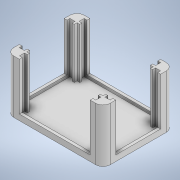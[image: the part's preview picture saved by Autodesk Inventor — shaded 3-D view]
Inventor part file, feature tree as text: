
AUTODESK INVENTOR PART (.ipt)
format: ipt  version: 2021 (Build 250183000, 183)  size: 203,776 bytes
history: native  units: mm
features: extrude x3, sketch x2, projected_geometry x1
ambient origin geometry x8: Origin, YZ Plane, XZ Plane, XY Plane, X Axis, Y Axis, Z Axis, Center Point
bodies: Volumenkörper1 (feature_tree)
feature tree (6):
  extrude  "Extrusion1"  Depth=49.0mm
  sketch  "Skizze2"  dims[d2=5.0mm d3=2.0mm d4=0.0mm d5=3.5mm d6=2.0mm d7=35.0mm d9=2.0mm d10=2.0mm d11=2.0mm d12=2.0mm d13=0.0mm d14=35.0mm d15=0.0mm]
  extrude  "Extrusion2"  Depth=2.0mm TaperAngle=0.0deg
  extrude  "Extrusion3"  Depth=3.5mm
  sketch  "Skizze1"  dims[d0=67.0mm d1=49.0mm]
  projected_geometry  "Projizierte Kontur1"
